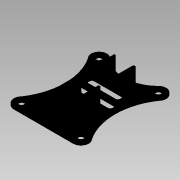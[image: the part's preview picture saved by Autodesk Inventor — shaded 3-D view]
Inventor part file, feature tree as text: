
AUTODESK INVENTOR PART (.ipt)
format: ipt  version: 2015 SP1 (Build 190203100, 203)  size: 382,464 bytes
history: native  units: mm
features: extrude x10, sketch x6, projected_geometry x6, reference x3
ambient origin geometry x8: Origin, YZ Plane, XZ Plane, XY Plane, X Axis, Y Axis, Z Axis, Center Point
bodies: Body1 (feature_tree)
feature tree (25):
  extrude  "Extrusion14"  Depth=3.5mm
  extrude  "Extrusion15"  Depth=3.5mm
  extrude  "Extrusion16"  Depth=5.0mm
  extrude  "Extrusion17"  Depth=2.0mm
  extrude  "Extrusion18"  Depth=23.5mm
  extrude  "Extrusion19"  Depth=23.5mm
  extrude  "Extrusion20"  Depth=23.5mm
  sketch  "Sketch21"  dims[d219=12.747276mm d220=12.747276mm d235=6.458811mm d241=18.458811mm d242=18.458811mm d244=5.0mm]
  extrude  "Extrusion23"  Depth=23.5mm
  extrude  "Extrusion24"  Depth=23.5mm
  extrude  "Extrusion25"  Depth=23.5mm
  sketch  "Sketch1"  dims[d19=46.65mm d72=0.0mm d105=3.5mm]
  sketch  "Sketch14"  dims[d106=3.5mm d198=16.0mm]
  reference  "Reference1"
  reference  "Reference2"
  reference  "Reference3"
  sketch  "Sketch20"  dims[d199=8.65129mm]
  sketch  "Sketch23"  dims[d247=79.203871mm d248=2.0mm]
  projected_geometry  "Projected Loop5"
  projected_geometry  "Projected Loop6"
  projected_geometry  "Projected Loop7"
  projected_geometry  "Projected Loop8"
  sketch  "Sketch24"  dims[d249=3.5mm d250=2.5mm d251=2.5mm d252=146.323246mm d253=146.323245mm d258=6.00224mm d259=27.79742mm d260=69.254481mm d261=3.0mm d262=0.0mm d263=5.821895mm d264=5.821895mm d265=5.821895mm d266=46.987913mm d267=12.022738mm d268=63.629996mm d269=3.0mm d270=0.0mm d271=46.987914mm d272=12.02274mm d275=3.0mm d276=0.0mm d278=3.5mm d279=3.5mm d280=3.0mm d281=0.0mm d285=5.0mm d286=5.0mm d287=3.5mm d288=0.0mm d289=3.5mm d298=3.0mm d299=0.0mm d300=30.0mm d301=5.0mm d302=3.5mm d303=25.0mm d304=9.0mm d305=3.5mm d306=0.0mm d308=1.159189mm d309=16.5mm d310=13.5mm d311=13.5mm d312=16.5mm d317=23.5mm d318=0.0mm d319=47.0mm d320=0.0mm d321=23.5mm d322=0.0mm]
  projected_geometry  "Projected Loop9"
  projected_geometry  "Projected Loop10"
